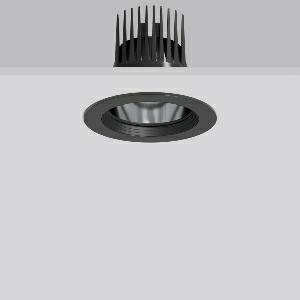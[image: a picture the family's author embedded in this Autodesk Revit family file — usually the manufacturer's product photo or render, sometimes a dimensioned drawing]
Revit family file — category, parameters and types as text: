
# Revit family: heledon_maxi_e_901785_003_2_49d5
name_source: partatom
category: Lighting Fixtures
units: mm (PartAtom-declared; Revit-internal decimal feet)

## family parameters
Cut with Voids When Loaded = No
Host = Face
Light Source = No
Part Type = Normal
Room Calculation Point = No
Round Connector Dimension = Use Diameter
Shared = No

## types (1)
- HELEDON maxi E (1 x LED Modul 927 bakery, 3400 lm, 2700)
    Apparent Load = 33 VA
    Approval mark = CE
    CIE Flux Codes = 100 100 100 100 100
    Color Rendering = 90
    Color Temperature = 2700
    Default Elevation = 1800 mm
    Description = Series: HELEDON maxi
Round recessed downlight. Housing: die-cast aluminium, powder-coated. Black plastic ring and recessed LED to prevent glare from the side. Optical assembly with reflector made of MIRO-Silver with 98% total light reflection for outstanding efficiency - can be changed without tools. Special LED for illumination of pastries included. Suitable for Recessed ceiling mounting. Installation without tools thanks to spring fastening system. Including separate LED converter with connecting cable 600 mm.High quality converter without flickering and stroboscopic effect. Through-wiring box (5 pole) available as accessory. The following accessories can be mounted without use of tools: interchangeable lenses, decorative glasses, honeycomb louvre, clear and frosted diffusers, white interchangeable plastic ring. 
Colour: deep black, matt (RAL 9005)
Diameter: 162 mm
Height: 3 mm
Cut-out diameter: 152 mm
Recess height: 200 mm
Luminaire: recess height: 135 mm
Lamp: LED
Socket: without socket
Colour temperature: bakery
Colour rendering index (CRI): 97
System power: 33 W
Rated luminous flux: 3400 lm
Luminous efficiency: 103 lm/W
Control gear: Regulated power supply
Protection class: II
Type of protection: IP 20
    Height = 0 mm  [stored 0 ft]
    Lamp = 1 x LED Modul 927 bakery
    Lamp Light Flux = 3400 lm
    Lamp count = 1
    Length = 162 mm
    Lifetime = 50000 h
    Luminous efficacy = 103 lm/W
    Manufacturer = RZB
    ModVariant = No
    Model = 901785.003.2
    Mounting Place = Ceiling
    Mounting Type = Recessed
    Number of Poles = 1
    OnlyDefault = Yes
    Power Factor = 1
    Product Name = HELEDON maxi E
    Product group = Recessed downlights
    ProductGroupID = 402
    Protection Class = Protection class II
    Protection Degree = IP 20
    RLX_Detail_Level = 1
    RLX_Emergency_Light_Flux = 0 lm
    RLX_Emergency_Type = 0
    RLX_Emergency_Type_DB = No
    RlxData = <blob elided: 123685 chars, md5=b6411849>
    Socket = socket
    Standby Power = 0 W
    System Light Flux = 3400 lm
    System Power = 33 W
    Type Comments = Product without accessories
    Type Image = 901662.003.jpg
    URL = http://relux.com
    VarID = ---
    Voltage = 230 V
    Voltage Range = 220-240 V
    Weight = 0.00 kg
    Width = 0 mm  [stored 0 ft]

note: [stored X ft] marks values corroborated as IEEE doubles in the binary element streams (Revit-internal decimal feet)

## geometry (parser evidence)
native form markers: Blend x4, Sweep x10
no freeform markers — native parametric forms only
